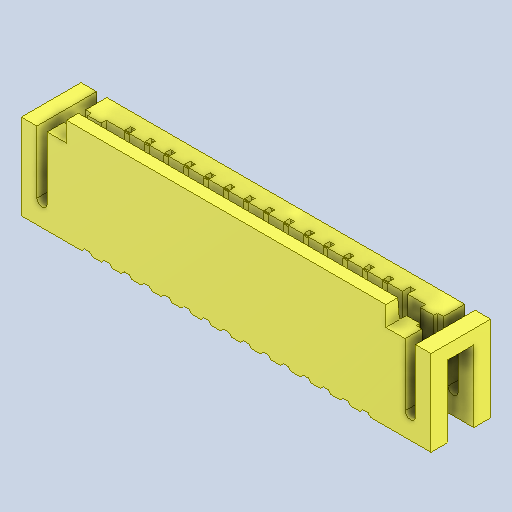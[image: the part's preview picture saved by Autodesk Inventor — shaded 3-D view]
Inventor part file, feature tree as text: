
AUTODESK INVENTOR PART (.ipt)
format: ipt  version: 2022 (Build 260153000, 153)  size: 421,888 bytes
history: mixed  units: in
note: dims shown in document units (in); Inventor stores cm internally (conversion verified against a paired STEP export)
features: mirror x1, imported_body x1
ambient origin geometry x8: Origin, YZ Plane, XZ Plane, XY Plane, X Axis, Y Axis, Z Axis, Center Point
bodies: Solid1 (imported_parasolid)
feature tree (2):
  mirror  "Mirror5"
  imported_body  NMx_Import_Brep_tag  [imported B-rep: ~395 faces, bbox_mm=[20.6, 5.3, 3.0]]
